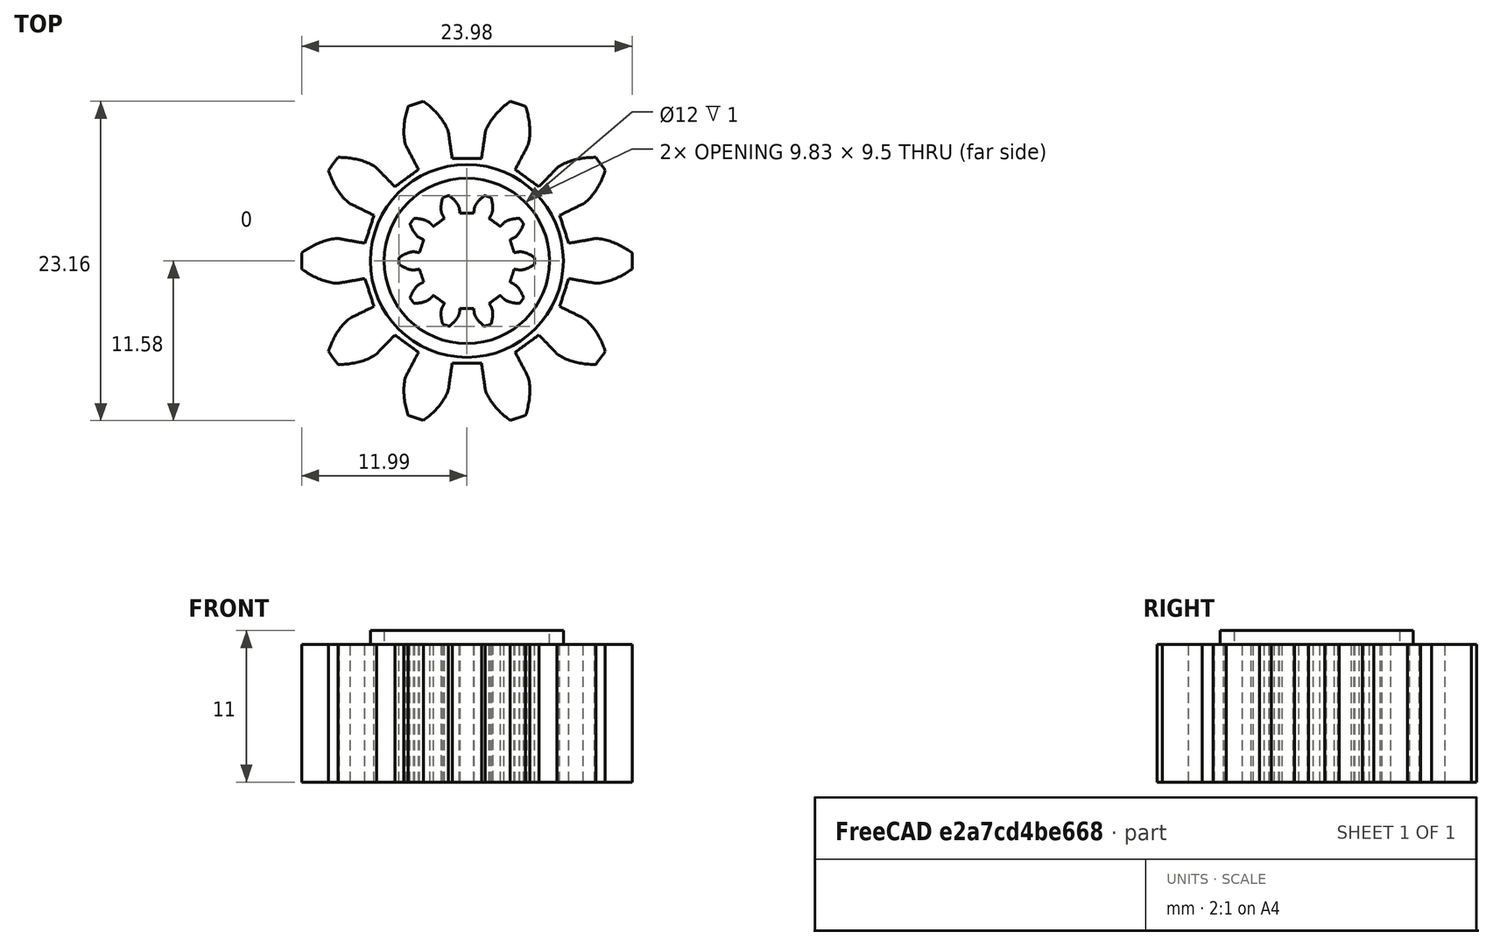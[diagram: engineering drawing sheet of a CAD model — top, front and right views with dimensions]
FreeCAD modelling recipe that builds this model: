
FCSTD DOCUMENT  (FreeCAD 0.17R13522 (Git))
Label: GearboxMotorCouplingGear
License: All rights reserved
LicenseURL: http://en.wikipedia.org/wiki/All_rights_reserved
objects: Part::FeaturePython×2, Part::Cut×1, Sketcher::SketchObject×1, PartDesign::Pad×1, PartDesign::Body×1, App::Part×1
note: 7 computed .brp shape members not serialized (recipe doc carries the construction recipe); baked Part::Feature solids carry a one-line shape summary decoded from their .brp

FEATURE [Part::FeaturePython] InvoluteGear002  # WARN: FeaturePython — macro-defined, semantics opaque (R4)
  backlash = 0
  beta = 0
  clearance = 0.25
  double_helix = false
  head = 0
  height = 10
  module = 2
  numpoints = 6
  pressure_angle = 20
  reversed_backlash = false
  shift = 0
  simple = false
  teeth = 10
  undercut = false
FEATURE [Part::FeaturePython] InvoluteGear003  # WARN: FeaturePython — macro-defined, semantics opaque (R4)
  backlash = 0
  beta = 0
  clearance = -0.25
  double_helix = false
  head = 0
  height = 10
  module = 0.82
  numpoints = 6
  pressure_angle = 20
  reversed_backlash = false
  shift = 0
  simple = false
  teeth = 10
  undercut = false
FEATURE [Part::Cut] Cut
  Base = -> InvoluteGear002
  Tool = -> InvoluteGear003
FEATURE [Sketcher::SketchObject] Sketch001  label="Sketch"
  MapMode = 5
  Placement = pos=(0,0,10) rot=(0,0,1;0rad)
  Support = -> [Cut]
  sketch-geometry (2):
    g0: Circle CenterX=0 CenterY=0 CenterZ=0 NormalX=0 NormalY=0 NormalZ=1 AngleXU=0 Radius=7
    g1: Circle CenterX=0 CenterY=0 CenterZ=0 NormalX=0 NormalY=0 NormalZ=1 AngleXU=0 Radius=6
  constraints (4):
    c: Coincident(g0,g-1)
    c: Coincident(g1,g-1)
    c: Radius(g1) = 6
    c: Radius(g0) = 7
FEATURE [PartDesign::Pad] Pad001  label="Pad"
  Length = 1
  Length2 = 100
  Profile = -> Sketch001
  Type = 0
FEATURE [PartDesign::Body] Body001  label="Body"
  Group = -> [Sketch001,Pad001]
  Origin = -> Origin003
  Tip = -> Pad001
FEATURE [App::Part] Part001  label="Part"
  Group = -> [InvoluteGear002,InvoluteGear003,Cut,Body001]
  License = CC BY 3.0
  LicenseURL = http://creativecommons.org/licenses/by/3.0/
  Origin = -> Origin002
